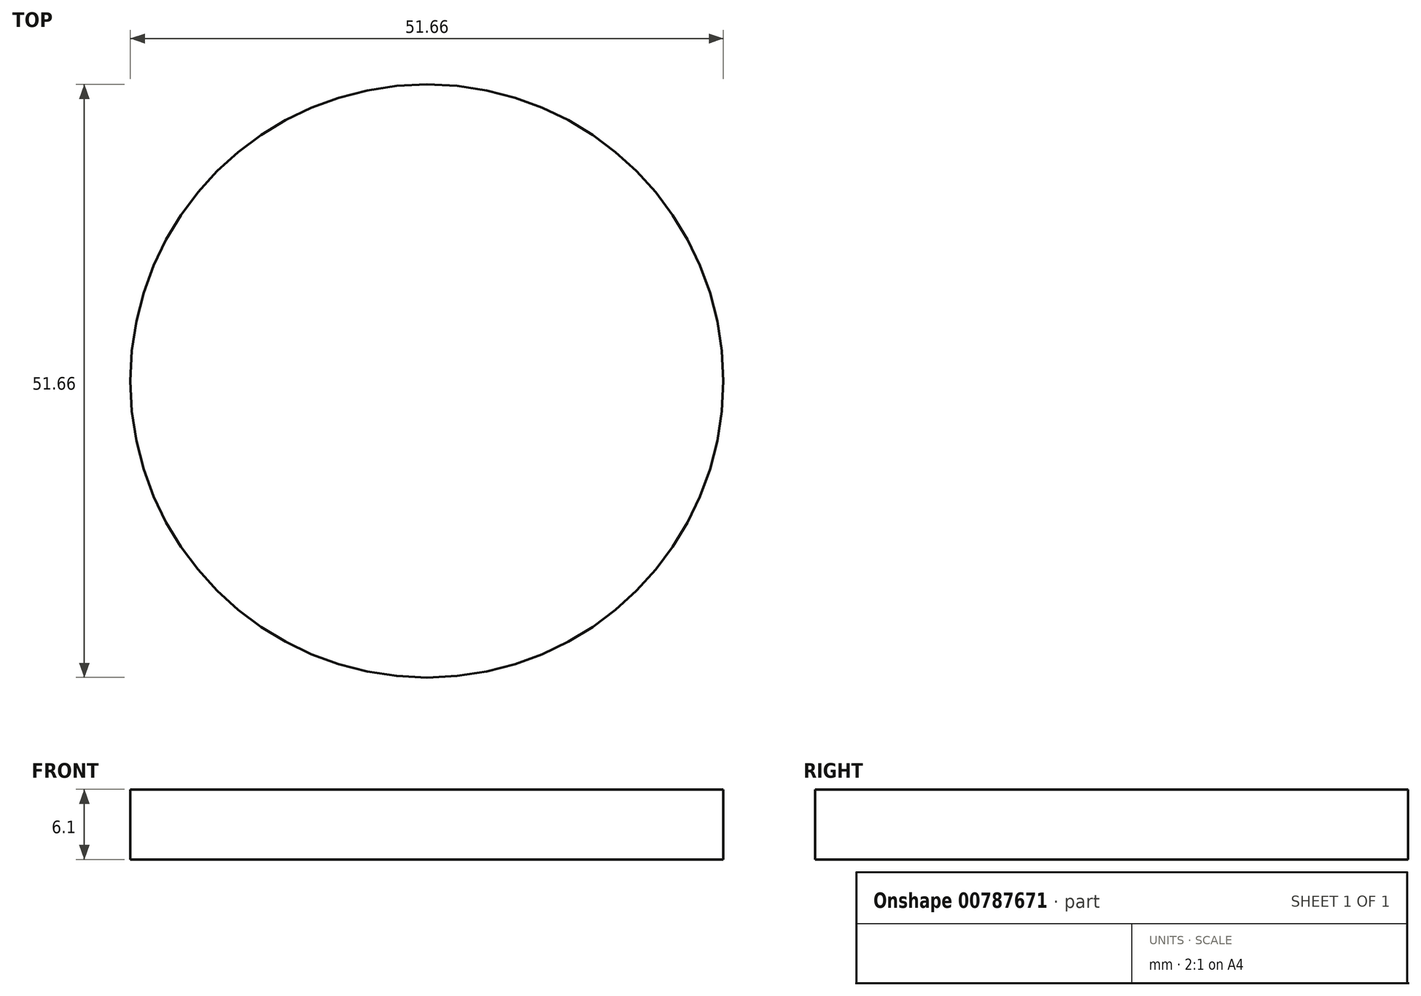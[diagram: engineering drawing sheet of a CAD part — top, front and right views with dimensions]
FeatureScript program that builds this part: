
annotation { "Feature Type Name" : "Feature", "Feature Type Description" : "" }
export const myFeature = defineFeature(function(context is Context, id is Id, definition is map)
    precondition{}
    {
        {
            var Q0;
            Q0=qCreatedBy(makeId("Top.planeOp"),FACE);
            var sketch = newSketch(context, id + "F0", { "sketchPlane" : qUnion([Q0])});
            skCircle(sketch, "E0", {"center": v(0, 0) * mm, "radius": 25.83 * mm});
            skSolve(sketch);
        }
        {
            var Q0;
            Q0 = qSketchRegion(id + "F0", true);
            extrude(context, id + "F1", {"entities" : qUnion([Q0]), "depth" : 6.1 * mm, "offsetDistance" : 25.4 * mm});
        }
    });
